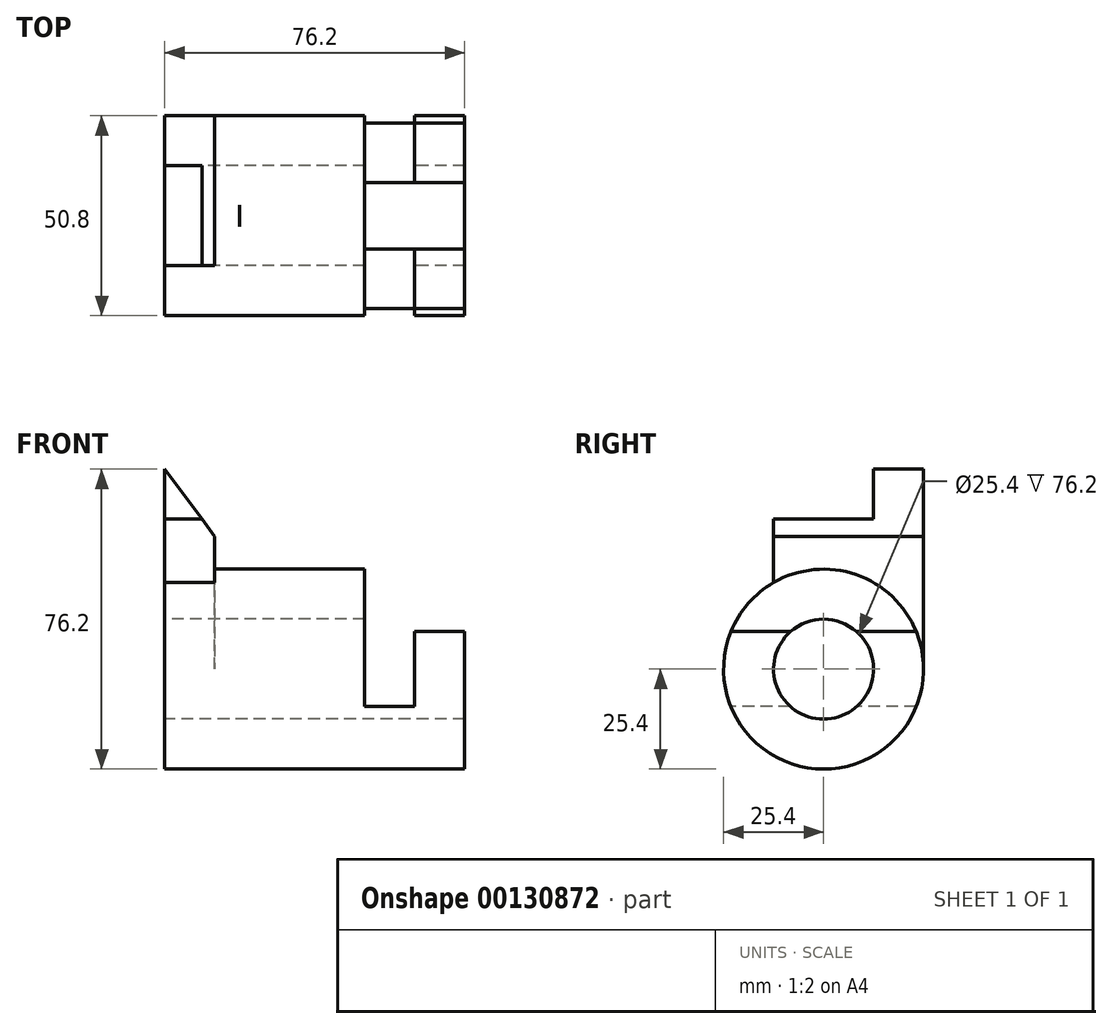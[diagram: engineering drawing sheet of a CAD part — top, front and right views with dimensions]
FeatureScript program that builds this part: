
annotation { "Feature Type Name" : "Feature", "Feature Type Description" : "" }
export const myFeature = defineFeature(function(context is Context, id is Id, definition is map)
    precondition{}
    {
        {
            var Q0;
            Q0=qCreatedBy(makeId("Right.planeOp"),FACE);
            var sketch = newSketch(context, id + "F0", { "sketchPlane" : qUnion([Q0])});
            skCircle(sketch, "E0", {"center": v(0, 0) * mm, "radius": 12.7 * mm});
            skLineSegment(sketch, "E1", {"start": v(0, 0) * mm, "end": v(0, 12.7) * mm, "construction": true});
            skCircle(sketch, "E2", {"center": v(0, 0) * mm, "radius": 25.4 * mm});
            skLineSegment(sketch, "E3", {"start": v(0, 0) * mm, "end": v(0, 25.4) * mm, "construction": true});
            skPoint(sketch, "E3.endSnap0", {"position": v(0, 6.35) * mm});
            skLineSegment(sketch, "E4", {"start": v(25.4, 0) * mm, "end": v(25.4, 50.8) * mm});
            skLineSegment(sketch, "E5", {"start": v(25.4, 50.8) * mm, "end": v(12.7, 50.8) * mm});
            skLineSegment(sketch, "E6", {"start": v(12.7, 50.8) * mm, "end": v(12.7, 38.1) * mm});
            skLineSegment(sketch, "E7", {"start": v(12.7, 38.1) * mm, "end": v(-12.7, 38.1) * mm});
            skLineSegment(sketch, "E8", {"start": v(-12.7, 38.1) * mm, "end": v(-12.7, 22) * mm});
            skSolve(sketch);
        }
        {
            var Q0;
            Q0 = qSketchRegion(id + "F0", true);
            extrude(context, id + "F1", {"entities" : qUnion([Q0]), "depth" : 76.2 * mm});
        }
        {
            var Q0;
            Q0=qCreatedBy(makeId("Front.planeOp"),FACE);
            var sketch = newSketch(context, id + "F2", { "sketchPlane" : qUnion([Q0])});
            skLineSegment(sketch, "E9", {"start": v(76.2, 25.4) * mm, "end": v(76.2, 9.53) * mm, "construction": true});
            skLineSegment(sketch, "E10", {"start": v(63.5, 25.4) * mm, "end": v(63.5, -9.53) * mm, "construction": true});
            skLineSegment(sketch, "E11", {"start": v(76.2, 25.4) * mm, "end": v(50.8, 25.4) * mm, "construction": true});
            skLineSegment(sketch, "E12", {"start": v(50.8, 25.4) * mm, "end": v(50.8, -9.53) * mm});
            skLineSegment(sketch, "E13", {"start": v(50.8, -9.53) * mm, "end": v(63.5, -9.53) * mm});
            skLineSegment(sketch, "E14", {"start": v(76.2, 9.53) * mm, "end": v(63.5, 9.53) * mm});
            skLineSegment(sketch, "E15", {"start": v(63.5, 9.53) * mm, "end": v(63.5, -9.53) * mm});
            skLineSegment(sketch, "E16", {"start": v(50.8, 25.4) * mm, "end": v(63.5, 25.4) * mm});
            skLineSegment(sketch, "E17", {"start": v(76.2, 9.53) * mm, "end": v(76.2, 25.4) * mm});
            skLineSegment(sketch, "E18", {"start": v(76.2, 25.4) * mm, "end": v(50.8, 25.4) * mm});
            skLineSegment(sketch, "E19", {"start": v(12.7, 25.4) * mm, "end": v(76.2, 25.4) * mm});
            skSolve(sketch);
        }
        {
            var Q0;
            Q0 = qSketchRegion(id + "F2", true);
            extrude(context, id + "F3", {"entities" : qUnion([Q0]), "operationType" : NewBodyOperationType.REMOVE, "endBound" : BoundingType.THROUGH_ALL, "oppositeDirection" : true, "depth" : 25.4 * mm, "hasSecondDirection" : true, "secondDirectionOppositeDirection" : false, "secondDirectionDepth" : 25.4 * mm});
        }
        {
            var Q0;
            {var subQ0=sQuery(id+"F0.wireOp",EDGE,"E7");var subQ1=sQuery(id+"F0.wireOp",EDGE,"E6");var subQ2=sQuery(id+"F0.wireOp",EDGE,"E5");var subQ3=sQuery(id+"F0.wireOp",EDGE,"E4");var subQ4=sQuery(id+"F0.wireOp",EDGE,"E8");Q0=makeQuery(id+"F3.boolean.opBoolean","SPLIT",FACE,{"disambiguationData":[TD([makeQuery(id+"F1.opExtrude","SWEPT_FACE",FACE,{"disambiguationData":[OSD([subQ2])]})])],"derivedFrom":makeQuery(id+"F1.opExtrude","CAP_FACE",FACE,{"disambiguationData":[OSD([sQuery(id+"F0.wireOp",EDGE,"E0"),sQuery(id+"F0.wireOp",EDGE,"E2"),subQ3,subQ2,subQ1,subQ0,subQ4])],"isStart":false})});}
            var sketch = newSketch(context, id + "F4", { "sketchPlane" : qUnion([Q0])});
            skArc(sketch, "E20", {"start": v(25.4, 0) * mm, "mid": v(12.7, 22) * mm, "end": v(-12.7, 22) * mm});
            skLineSegment(sketch, "E21.0", {"start": v(-12.7, 38.1) * mm, "end": v(-12.7, 22) * mm});
            skLineSegment(sketch, "E22.0", {"start": v(12.7, 38.1) * mm, "end": v(-12.7, 38.1) * mm});
            skLineSegment(sketch, "E23.0", {"start": v(25.4, 50.8) * mm, "end": v(12.7, 50.8) * mm});
            skLineSegment(sketch, "E24.0", {"start": v(12.7, 50.8) * mm, "end": v(12.7, 38.1) * mm});
            skLineSegment(sketch, "E25.0", {"start": v(25.4, 25.4) * mm, "end": v(25.4, 50.8) * mm});
            skLineSegment(sketch, "E26.0", {"start": v(25.4, 25.4) * mm, "end": v(25.4, 0) * mm});
            skSolve(sketch);
        }
        {
            var Q0;
            Q0 = qSketchRegion(id + "F4", true);
            extrude(context, id + "F5", {"entities" : qUnion([Q0]), "operationType" : NewBodyOperationType.REMOVE, "oppositeDirection" : true, "depth" : 63.5 * mm});
        }
        {
            var Q0;
            Q0=qCreatedBy(makeId("Front.planeOp"),FACE);
            var sketch = newSketch(context, id + "F6", { "sketchPlane" : qUnion([Q0])});
            skLineSegment(sketch, "E27", {"start": v(19.05, 25.26) * mm, "end": v(0, 50.8) * mm});
            skLineSegment(sketch, "E28", {"start": v(0, 50.8) * mm, "end": v(19.05, 50.8) * mm});
            skLineSegment(sketch, "E29", {"start": v(19.05, 25.26) * mm, "end": v(19.05, 50.8) * mm});
            skLineSegment(sketch, "E30", {"start": v(0, 0) * mm, "end": v(76.54, 0) * mm, "construction": true});
            skLineSegment(sketch, "E31", {"start": v(19.05, 25.26) * mm, "end": v(37.89, 0) * mm, "construction": true});
            skSolve(sketch);
        }
        {
            var Q0;
            Q0 = qSketchRegion(id + "F6", true);
            extrude(context, id + "F7", {"entities" : qUnion([Q0]), "operationType" : NewBodyOperationType.REMOVE, "oppositeDirection" : true, "depth" : 25.4 * mm, "hasSecondDirection" : true, "secondDirectionOppositeDirection" : false, "secondDirectionDepth" : 25.4 * mm});
        }
    });
